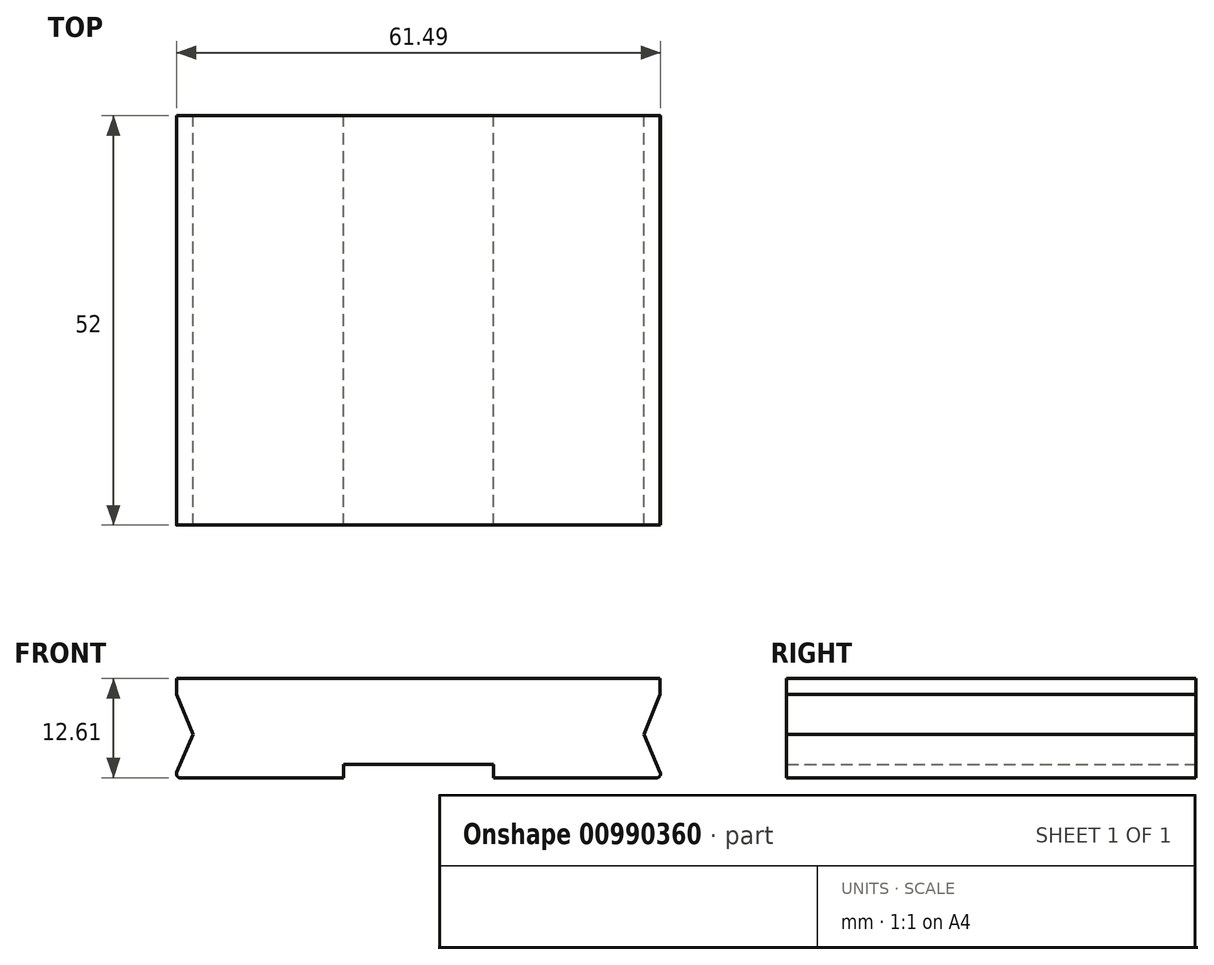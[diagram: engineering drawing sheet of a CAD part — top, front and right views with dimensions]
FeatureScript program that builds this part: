
annotation { "Feature Type Name" : "Feature", "Feature Type Description" : "" }
export const myFeature = defineFeature(function(context is Context, id is Id, definition is map)
    precondition{}
    {
        {
            var Q0;
            Q0=qCreatedBy(makeId("Front.planeOp"),FACE);
            var sketch = newSketch(context, id + "F0", { "sketchPlane" : qUnion([Q0])});
            skLineSegment(sketch, "E0", {"start": v(-39.13, 9.76) * mm, "end": v(-37.07, 14.57) * mm});
            skLineSegment(sketch, "E1", {"start": v(20.23, 14.57) * mm, "end": v(22.28, 9.76) * mm});
            skPoint(sketch, "E2.visualSharp", {"position": v(22.58, 9.07) * mm});
            skArc(sketch, "E2.filletArc", {"start": v(21.82, 9.07) * mm, "mid": v(22.24, 9.29) * mm, "end": v(22.28, 9.76) * mm});
            skPoint(sketch, "E3.visualSharp", {"position": v(-39.42, 9.07) * mm});
            skArc(sketch, "E3.filletArc", {"start": v(-39.13, 9.76) * mm, "mid": v(-39.08, 9.29) * mm, "end": v(-38.67, 9.07) * mm});
            skLineSegment(sketch, "E4", {"start": v(-38.67, 9.07) * mm, "end": v(-17.97, 9.07) * mm});
            skLineSegment(sketch, "E5", {"start": v(-17.97, 9.07) * mm, "end": v(-17.97, 10.77) * mm});
            skLineSegment(sketch, "E6", {"start": v(1.12, 10.77) * mm, "end": v(1.12, 9.07) * mm});
            skLineSegment(sketch, "E7", {"start": v(1.12, 9.07) * mm, "end": v(21.82, 9.07) * mm});
            skLineSegment(sketch, "E8", {"start": v(-17.97, 10.77) * mm, "end": v(1.12, 10.77) * mm});
            skLineSegment(sketch, "E9", {"start": v(-39.13, 21.68) * mm, "end": v(22.28, 21.68) * mm});
            skLineSegment(sketch, "E10", {"start": v(22.28, 21.68) * mm, "end": v(22.28, 19.68) * mm});
            skLineSegment(sketch, "E11", {"start": v(20.23, 14.57) * mm, "end": v(22.28, 19.68) * mm});
            skLineSegment(sketch, "E12", {"start": v(-39.13, 21.68) * mm, "end": v(-39.13, 19.68) * mm});
            skLineSegment(sketch, "E13", {"start": v(-39.13, 19.68) * mm, "end": v(-37.07, 14.57) * mm});
            skSolve(sketch);
        }
        {
            var Q0;
            Q0=qSketchRegion(id+"F0",true);
            extrude(context, id + "F1", {"entities" : qUnion([Q0]), "depth" : 52 * mm, "offsetDistance" : 25 * mm});
        }
    });
